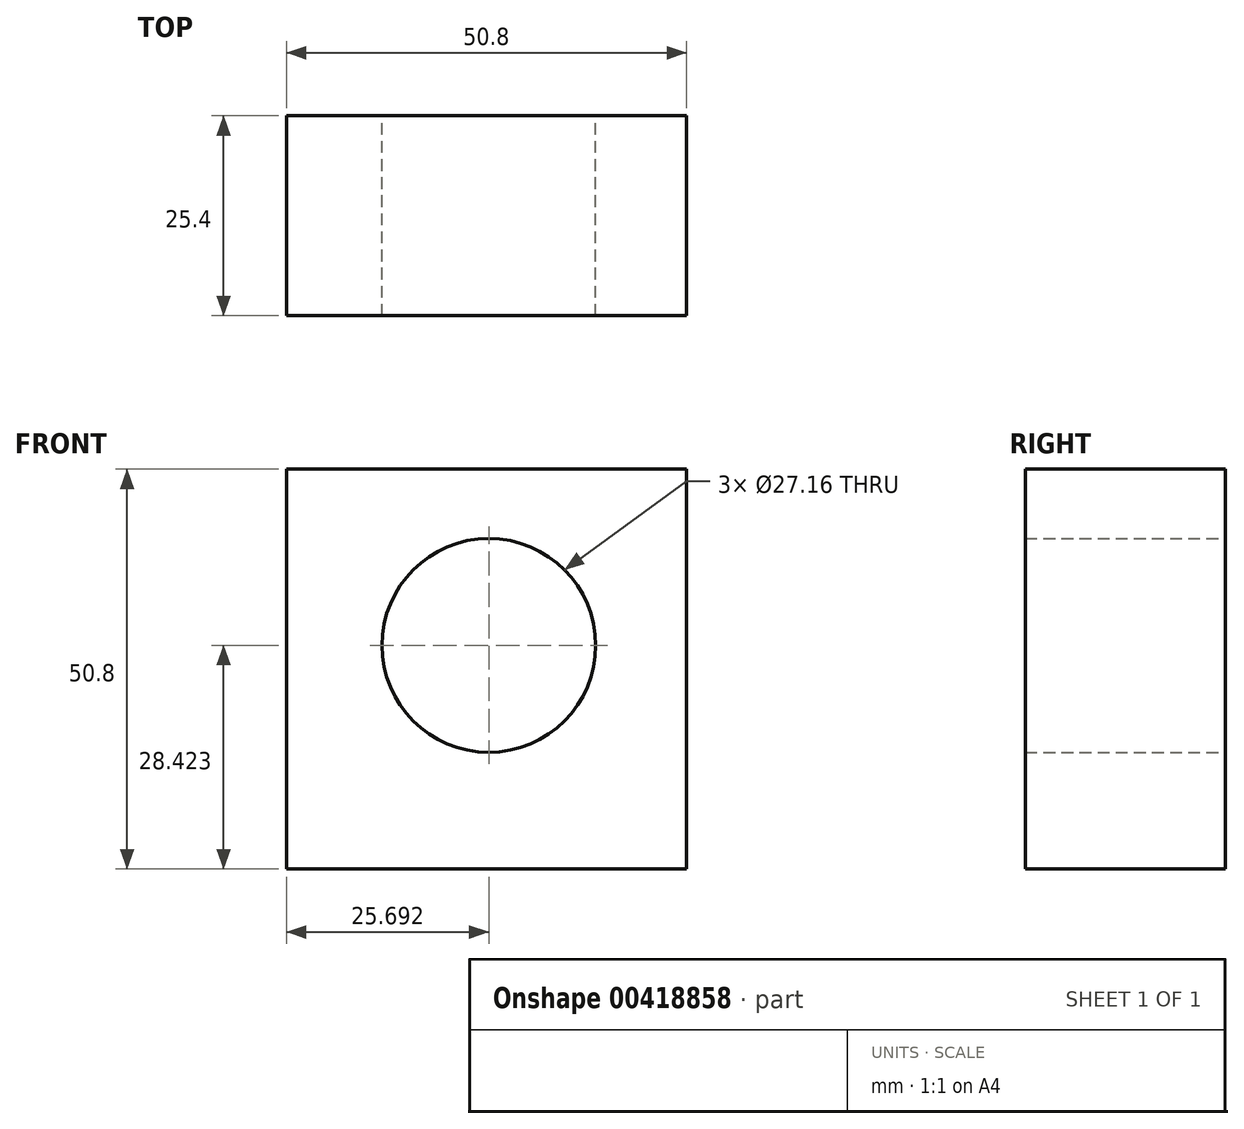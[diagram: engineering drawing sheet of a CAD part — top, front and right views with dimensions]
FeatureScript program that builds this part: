
annotation { "Feature Type Name" : "Feature", "Feature Type Description" : "" }
export const myFeature = defineFeature(function(context is Context, id is Id, definition is map)
    precondition{}
    {
        {
            var Q0;
            Q0=qCreatedBy(makeId("Front.planeOp"),FACE);
            var sketch = newSketch(context, id + "F0", { "sketchPlane" : qUnion([Q0])});
            skLineSegment(sketch, "E0.bottom", {"start": v(0, 0) * mm, "end": v(50.8, 0) * mm});
            skLineSegment(sketch, "E0.top", {"start": v(0, 50.8) * mm, "end": v(50.8, 50.8) * mm});
            skLineSegment(sketch, "E0.left", {"start": v(0, 0) * mm, "end": v(0, 50.8) * mm});
            skLineSegment(sketch, "E0.right", {"start": v(50.8, 0) * mm, "end": v(50.8, 50.8) * mm});
            skCircle(sketch, "E1", {"center": v(25.7, 28.42) * mm, "radius": 13.58 * mm});
            skSolve(sketch);
        }
        {
            var Q0;
            Q0=makeQuery(id+"F0.imprint","IMPRINT",FACE,{"disambiguationData":[TD([[makeQuery(id+"F0.imprint","IMPRINT",EDGE,{"derivedFrom":sQuery(id+"F0.wireOp",EDGE,"E0.bottom")}),1.0]])]});
            extrude(context, id + "F1", {"entities" : qUnion([Q0]), "depth" : 25.4 * mm});
        }
    });
